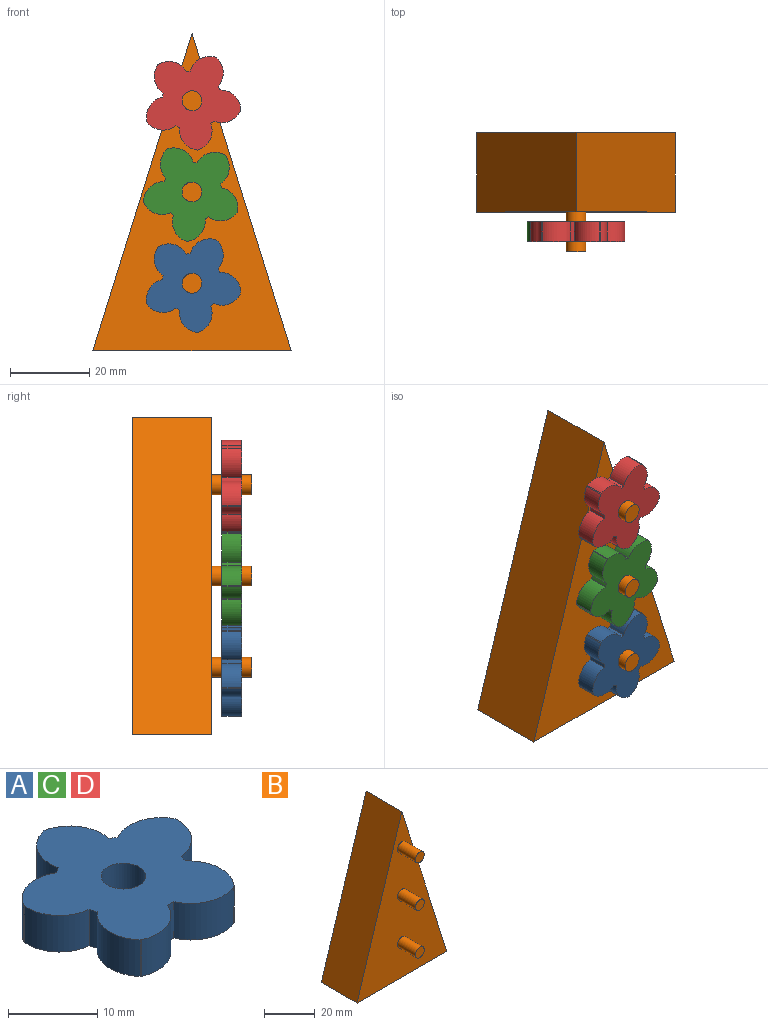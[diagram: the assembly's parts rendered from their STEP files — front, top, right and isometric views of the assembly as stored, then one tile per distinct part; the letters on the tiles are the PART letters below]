
ASSEMBLY  parts=4 mates=3
PART A: 23 faces, bbox 23.9x23.1x5 mm
  f0: cylinder r=5.12mm len=6.15mm, axis (0,0,-1), area 40.5mm2, adj f1,f19,f20,f21
  f1: cylinder r=7.5mm len=5mm, axis (0,0,-1), area 5.1mm2, adj f0,f2,f20,f21
  f2: cylinder r=5.12mm len=7.05mm, axis (0,0,-1), area 40.5mm2, adj f1,f3,f20,f21
  f3: plane 5x0.19mm, normal (-0.95,0.31,0), area 1mm2, adj f2,f4,f20,f21
  f4: cylinder r=5.12mm len=5.6mm, axis (0,0,-1), area 40.5mm2, adj f3,f5,f20,f21
  f5: cylinder r=7.5mm len=5mm, axis (0,0,-1), area 5.1mm2, adj f4,f6,f20,f21
  f6: cylinder r=5.12mm len=7.26mm, axis (0,0,-1), area 40.5mm2, adj f5,f7,f20,f21
  f7: plane 5x0.16mm, normal (-0.59,-0.81,0), area 1mm2, adj f6,f8,f20,f21
  f8: cylinder r=5.12mm len=6.76mm, axis (0,0,-1), area 40.5mm2, adj f7,f9,f20,f21
  f9: cylinder r=7.5mm len=5mm, axis (0,0,-1), area 5.1mm2, adj f8,f10,f20,f21
  f10: cylinder r=5.12mm len=6.76mm, axis (0,0,-1), area 40.5mm2, adj f9,f11,f20,f21
  f11: plane 5x0.16mm, normal (0.59,-0.81,0), area 1mm2, adj f10,f12,f20,f21
  f12: cylinder r=5.12mm len=7.26mm, axis (0,0,-1), area 40.5mm2, adj f11,f13,f20,f21
  f13: cylinder r=7.5mm len=5mm, axis (0,0,-1), area 5.1mm2, adj f12,f14,f20,f21
  f14: cylinder r=5.12mm len=5.6mm, axis (0,0,-1), area 40.5mm2, adj f13,f15,f20,f21
  f15: plane 5x0.19mm, normal (0.95,0.31,0), area 1mm2, adj f14,f16,f20,f21
  f16: cylinder r=5.12mm len=7.05mm, axis (0,0,-1), area 40.5mm2, adj f15,f17,f20,f21
  f17: cylinder r=7.5mm len=5mm, axis (0,0,-1), area 5.1mm2, adj f16,f18,f20,f21
  f18: cylinder r=5.12mm len=6.15mm, axis (0,0,-1), area 40.5mm2, adj f17,f19,f20,f21
  f19: plane 5x0.2mm, normal (0,1,0), area 1mm2, adj f0,f18,f20,f21
  f20: plane 23.89x23.1mm, normal (0,0,1), area 327.8mm2, adj f0,f1,f2,f3,f4,f5,f6,f7
  f21: plane 23.89x23.1mm, normal (0,0,-1), area 327.8mm2, adj f0,f1,f2,f3,f4,f5,f6,f7
  f22: cylinder r=2.5mm len=5mm, axis (0,0,1), area 78.5mm2, adj f20,f21
PART B: 11 faces, bbox 50x30x80 mm
  f0: plane 50x20mm, normal (0,0,-1), area 1000mm2, adj f1,f2,f3,f4
  f1: plane 80x25mm, normal (0.95,0,0.3), area 1676.3mm2, adj f0,f2,f3,f4
  f2: plane 80x25mm, normal (-0.95,0,0.3), area 1676.3mm2, adj f0,f1,f3,f4
  f3: plane 80x50mm, normal (0,1,0), area 2000mm2, adj f0,f1,f2
  f4: plane 80x50mm, normal (0,-1,0), area 1941.1mm2, adj f0,f1,f2,f5,f7,f9
  f5: cylinder r=2.5mm len=10mm, axis (0,1,0), area 157.1mm2, adj f4,f6
  f6: plane 5x5mm, normal (0,-1,0), area 19.6mm2, adj f5
  f7: cylinder r=2.5mm len=10mm, axis (0,1,0), area 157.1mm2, adj f4,f8
  f8: plane 5x5mm, normal (0,-1,0), area 19.6mm2, adj f7
  f9: cylinder r=2.5mm len=10mm, axis (0,1,0), area 157.1mm2, adj f4,f10
  f10: plane 5x5mm, normal (0,-1,0), area 19.6mm2, adj f9
PART C: same geometry as A
PART D: same geometry as A
PLACE A rot(axis=(-0.18,-0.7,-0.7),159.7deg) t=(1.86,2.5,-18.09)mm
PLACE B t=(1.86,10,4.91)mm fixed
PLACE C rot(axis=(-1,0.05,0.05),90.2deg) t=(1.86,2.5,4.91)mm
PLACE D rot(axis=(0.94,0.24,-0.24),93.6deg) t=(1.86,7.5,27.91)mm
MATE revolute B.f7 <-> C.f1  axis (0,1,0) through (1.86,5,4.91)mm
MATE revolute B.f5 <-> D.f1  axis (0,1,0) through (1.86,5,27.91)mm
MATE revolute A.f1 <-> B.f9  axis (0,1,0) through (1.86,5,-18.09)mm
